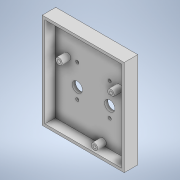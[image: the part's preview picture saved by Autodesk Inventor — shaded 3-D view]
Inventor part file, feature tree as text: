
AUTODESK INVENTOR PART (.ipt)
format: ipt  version: 2021 (Build 250183000, 183)  size: 260,608 bytes
history: native  units: mm
features: extrude x10, sketch x9, projected_geometry x4, plane x1
ambient origin geometry x8: Origin, YZ Plane, XZ Plane, XY Plane, X Axis, Y Axis, Z Axis, Center Point
bodies: Body1 (feature_tree)
feature tree (24):
  plane  "Work Plane1"
  sketch  "Sketch1"  dims[d0=2.9mm d1=2.9mm]
  extrude  "Extrusion1"  Depth=2.9mm
  extrude  "Extrusion2"  Depth=3.0mm TaperAngle=0.0deg
  extrude  "Extrusion3"  Depth=6.0mm
  extrude  "Extrusion5"  Depth=3.0mm TaperAngle=0.0deg
  extrude  "Extrusion6"  Depth=2.9mm
  extrude  "Extrusion7"  Depth=2.9mm
  extrude  "Extrusion8"  Depth=3.0mm TaperAngle=0.0deg
  extrude  "Extrusion9"  Depth=0.5mm
  extrude  "Extrusion10"  Depth=10.0mm
  extrude  "Extrusion11"  Depth=10.0mm TaperAngle=0.0deg
  sketch  "Sketch2"  dims[d2=2.9mm d7=3.0mm d8=0.0mm]
  sketch  "Sketch3"  dims[d9=6.0mm d10=6.0mm]
  sketch  "Sketch5"  dims[d11=6.0mm d12=3.0mm d13=0.0mm]
  sketch  "Sketch6"  dims[d19=2.9mm d20=2.9mm]
  sketch  "Sketch7"  dims[d21=2.9mm d22=2.9mm]
  projected_geometry  "Projected Loop1"
  projected_geometry  "Projected Loop2"
  projected_geometry  "Projected Loop3"
  sketch  "Sketch8"  dims[d23=3.0mm d24=0.0mm d31=4.58mm d32=0.0mm]
  projected_geometry  "Projected Loop4"
  sketch  "Sketch9"  dims[d33=0.5mm d34=0.5mm]
  sketch  "Sketch10"  dims[d35=0.5mm d36=0.5mm d37=10.0mm d38=0.0mm d40=9.534mm d41=0.0mm d42=0.0mm d43=5.0mm d44=0.0mm d45=5.0mm d46=0.0mm d47=2.0mm d48=5.0mm d49=0.0mm d50=5.0mm d51=0.0mm]
